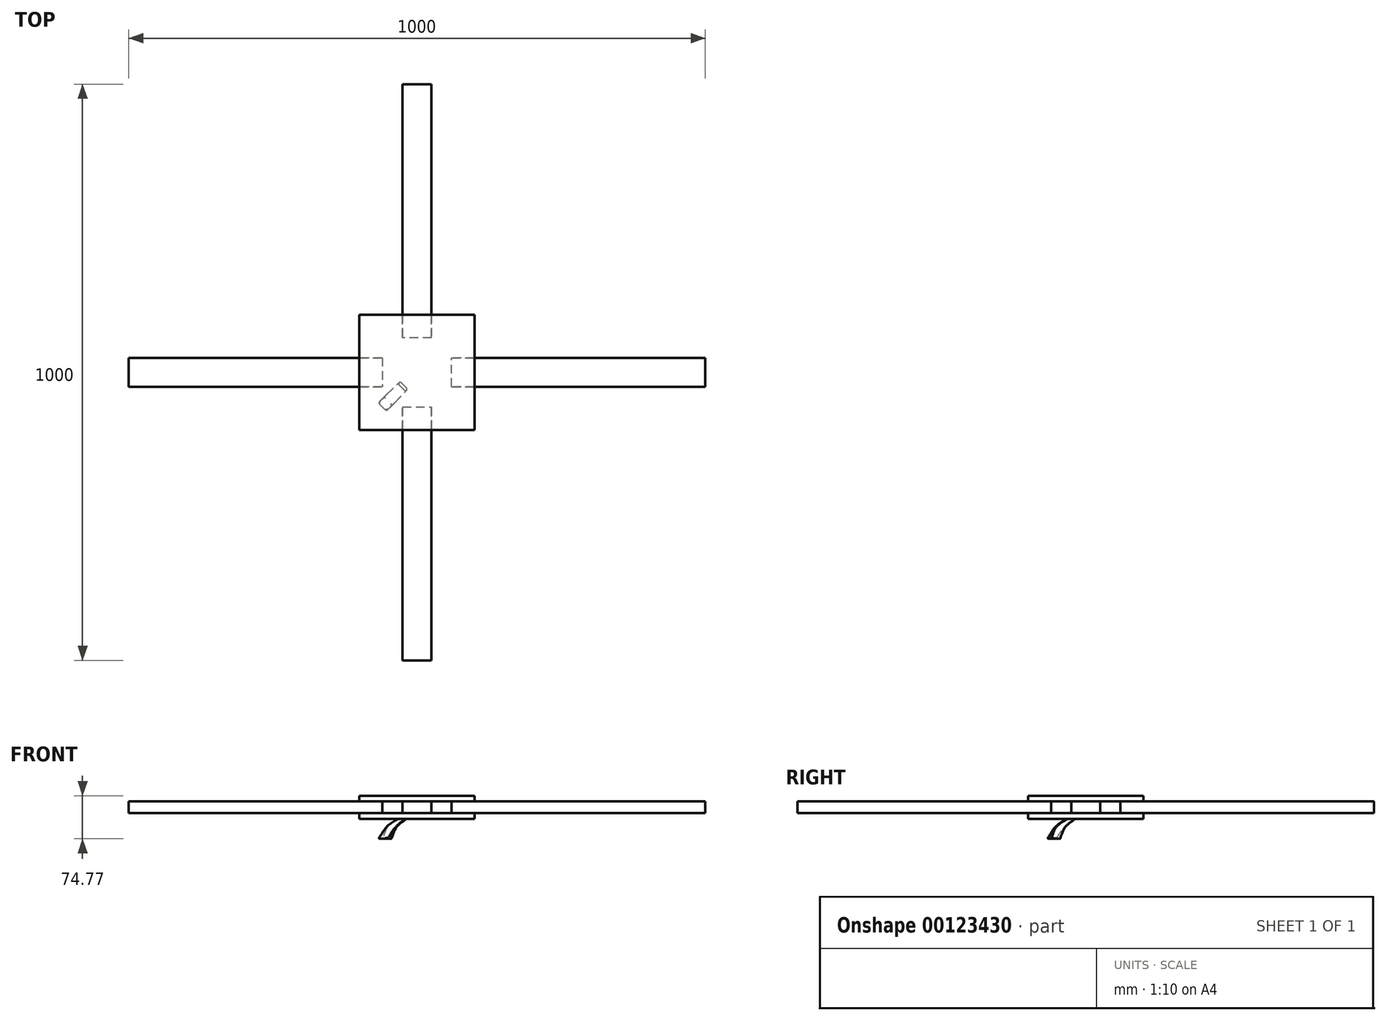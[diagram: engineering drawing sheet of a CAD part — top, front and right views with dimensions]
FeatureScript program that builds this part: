
annotation { "Feature Type Name" : "Feature", "Feature Type Description" : "" }
export const myFeature = defineFeature(function(context is Context, id is Id, definition is map)
    precondition{}
    {
        {
            var Q0;
            Q0=qCreatedBy(makeId("Top.planeOp"),FACE);
            var sketch = newSketch(context, id + "F0", { "sketchPlane" : qUnion([Q0])});
            skLineSegment(sketch, "E0.bottom", {"start": v(100, -100) * mm, "end": v(-100, -100) * mm});
            skLineSegment(sketch, "E0.top", {"start": v(100, 100) * mm, "end": v(-100, 100) * mm});
            skLineSegment(sketch, "E0.left", {"start": v(100, -100) * mm, "end": v(100, 100) * mm});
            skLineSegment(sketch, "E0.right", {"start": v(-100, -100) * mm, "end": v(-100, 100) * mm});
            skPoint(sketch, "E0.middle", {"position": v(0, 0) * mm});
            skSolve(sketch);
        }
        {
            var Q0;
            Q0 = qSketchRegion(id + "F0", true);
            extrude(context, id + "F1", {"entities" : qUnion([Q0]), "depth" : 40 * mm});
        }
        {
            var Q0;
            Q0=makeQuery(id+"F1.opExtrude","SWEPT_FACE",FACE,{"disambiguationData":[OSD([sQuery(id+"F0.wireOp",EDGE,"E0.bottom")])]});
            var sketch = newSketch(context, id + "F2", { "sketchPlane" : qUnion([Q0])});
            skLineSegment(sketch, "E1.bottom", {"start": v(-100, 30) * mm, "end": v(100, 30) * mm});
            skLineSegment(sketch, "E1.top", {"start": v(-100, 10) * mm, "end": v(100, 10) * mm});
            skLineSegment(sketch, "E1.left", {"start": v(-100, 30) * mm, "end": v(-100, 10) * mm});
            skLineSegment(sketch, "E1.right", {"start": v(100, 30) * mm, "end": v(100, 10) * mm});
            skSolve(sketch);
        }
        {
            var Q0;
            Q0 = qSketchRegion(id + "F2", true);
            var Q1;
            Q1=makeQuery(id+"F1.opExtrude","SWEPT_FACE",FACE,{"disambiguationData":[OSD([sQuery(id+"F0.wireOp",EDGE,"E0.top")])]});
            extrude(context, id + "F3", {"entities" : qUnion([Q0]), "operationType" : NewBodyOperationType.REMOVE, "endBound" : BoundingType.UP_TO_SURFACE, "oppositeDirection" : true, "endBoundEntityFace" : qUnion([Q1]), "depth" : 25 * mm});
        }
        {
            var Q0;
            Q0=makeQuery(id+"F3.boolean.opBoolean","COPY",FACE,{"derivedFrom":makeQuery(id+"F3.opExtrude","SWEPT_FACE",FACE,{"disambiguationData":[OSD([sQuery(id+"F2.wireOp",EDGE,"E1.top")])]})});
            var sketch = newSketch(context, id + "F4", { "sketchPlane" : qUnion([Q0])});
            skLineSegment(sketch, "E2.bottom", {"start": v(60, 25) * mm, "end": v(500, 25) * mm});
            skLineSegment(sketch, "E2.top", {"start": v(60, -25) * mm, "end": v(500, -25) * mm});
            skLineSegment(sketch, "E2.left", {"start": v(60, 25) * mm, "end": v(60, -25) * mm});
            skLineSegment(sketch, "E2.right", {"start": v(500, 25) * mm, "end": v(500, -25) * mm});
            skSolve(sketch);
        }
        {
            var Q0;
            Q0 = qSketchRegion(id + "F4", true);
            var Q1;
            Q1=makeQuery(id+"F3.boolean.opBoolean","COPY",FACE,{"derivedFrom":makeQuery(id+"F3.opExtrude","SWEPT_FACE",FACE,{"disambiguationData":[OSD([sQuery(id+"F2.wireOp",EDGE,"E1.bottom")])]})});
            extrude(context, id + "F5", {"entities" : qUnion([Q0]), "endBound" : BoundingType.UP_TO_SURFACE, "endBoundEntityFace" : qUnion([Q1]), "depth" : 25 * mm});
        }
        {
            var Q0;
            Q0=makeQuery(id+"F1.opExtrude","CAP_FACE",FACE,{"disambiguationData":[OSD([sQuery(id+"F0.wireOp",EDGE,"E0.bottom"),sQuery(id+"F0.wireOp",EDGE,"E0.top"),sQuery(id+"F0.wireOp",EDGE,"E0.left"),sQuery(id+"F0.wireOp",EDGE,"E0.right")])],"isStart":false});
            var sketch = newSketch(context, id + "F6", { "sketchPlane" : qUnion([Q0])});
            skCircle(sketch, "E3", {"center": v(0, 0) * mm, "radius": 26.92 * mm});
            skSolve(sketch);
        }
        {
            var Q0;
            Q0=makeQuery(id+"F5.opExtrude","SWEPT_BODY",BODY,{"disambiguationData":[OSD([sQuery(id+"F4.wireOp",EDGE,"E2.bottom"),sQuery(id+"F4.wireOp",EDGE,"E2.top"),sQuery(id+"F4.wireOp",EDGE,"E2.left"),sQuery(id+"F4.wireOp",EDGE,"E2.right")])]});
            var Q1;
            Q1=sQuery(id+"F6.wireOp",EDGE,"E3");
            circularPattern(context, id + "F7", {"entities" : qUnion([Q0]), "axis" : qUnion([Q1]), "angle" : 360 * degree, "instanceCount" : 4, "equalSpace" : true});
        }
        {
            var Q0;
            Q0=makeQuery(id+"F1.opExtrude","CAP_VERTEX",VERTEX,{"disambiguationData":[OSD([sQuery(id+"F0.wireOp",EDGE,"E0.bottom"),sQuery(id+"F0.wireOp",EDGE,"E0.right")])],"isStart":false});
            var Q1;
            Q1=makeQuery(id+"F1.opExtrude","CAP_VERTEX",VERTEX,{"disambiguationData":[OSD([sQuery(id+"F0.wireOp",EDGE,"E0.top"),sQuery(id+"F0.wireOp",EDGE,"E0.left")])],"isStart":false});
            var Q2;
            Q2=qCreatedBy(makeId("Origin.pointOp"),VERTEX);
            cPlane(context, id + "F8", {"entities" : qUnion([Q0, Q1, Q2]), "cplaneType" : CPlaneType.THREE_POINT, "offset" : 25 * mm, "width" : 150 * mm, "height" : 150 * mm});
        }
        {
            var Q0;
            Q0=qCreatedBy(id+"F8.planeOp",FACE);
            var sketch = newSketch(context, id + "F9", { "sketchPlane" : qUnion([Q0])});
            skFitSpline(sketch, "E4", {"points": [v(-37.62, 0) * mm, v(-65.27, -13) * mm, v(-86.01, -34.77) * mm], "startDerivative": vector(-58.46, -21.4) * mm, "endDerivative": vector(-38.3, -48.17) * mm});
            skLineSegment(sketch, "E5", {"start": v(-86.01, -34.77) * mm, "end": v(-70.8, -34.77) * mm});
            skFitSpline(sketch, "E6", {"points": [v(-70.8, -34.77) * mm, v(-59.74, -15.76) * mm, v(-32.43, 0) * mm], "startDerivative": vector(18.43, 44.7) * mm, "endDerivative": vector(57.15, 25.42) * mm});
            skLineSegment(sketch, "E7", {"start": v(-37.62, 0) * mm, "end": v(-32.43, 0) * mm});
            skSolve(sketch);
        }
        {
            var Q0;
            Q0 = qSketchRegion(id + "F9", true);
            extrude(context, id + "F10", {"entities" : qUnion([Q0]), "operationType" : NewBodyOperationType.ADD, "depth" : 10 * mm, "hasSecondDirection" : true, "secondDirectionOppositeDirection" : true, "secondDirectionDepth" : 10 * mm});
        }
        {
            var Q0;
            Q0=makeQuery(id+"F10.opExtrude","CAP_EDGE",EDGE,{"disambiguationData":[OSD([sQuery(id+"F9.wireOp",EDGE,"E4")])],"isStart":false});
            var Q1;
            Q1=makeQuery(id+"F10.opExtrude","CAP_EDGE",EDGE,{"disambiguationData":[OSD([sQuery(id+"F9.wireOp",EDGE,"E4")])],"isStart":true});
            var Q2;
            Q2=makeQuery(id+"F10.opExtrude","CAP_EDGE",EDGE,{"disambiguationData":[OSD([sQuery(id+"F9.wireOp",EDGE,"E6")])],"isStart":false});
            var Q3;
            Q3=makeQuery(id+"F10.opExtrude","CAP_EDGE",EDGE,{"disambiguationData":[OSD([sQuery(id+"F9.wireOp",EDGE,"E6")])],"isStart":true});
            fillet(context, id + "F11", {"entities" : qUnion([Q0, Q1, Q2, Q3]), "radius" : 3 * mm, "tangentPropagation" : true, "allowEdgeOverflow" : false});
        }
        {
            var Q0;
            Q0=makeQuery(id+"F10.opExtrude","SWEPT_FACE",FACE,{"disambiguationData":[OSD([sQuery(id+"F9.wireOp",EDGE,"E5")])]});
            fillet(context, id + "F12", {"entities" : qUnion([Q0]), "radius" : 1 * mm, "tangentPropagation" : true, "allowEdgeOverflow" : false});
        }
        {
            var Q0;
            Q0=makeQuery(id+"F1.opExtrude","CAP_FACE",FACE,{"disambiguationData":[OSD([sQuery(id+"F0.wireOp",EDGE,"E0.bottom"),sQuery(id+"F0.wireOp",EDGE,"E0.top"),sQuery(id+"F0.wireOp",EDGE,"E0.left"),sQuery(id+"F0.wireOp",EDGE,"E0.right")])],"isStart":false});
            var sketch = newSketch(context, id + "F13", { "sketchPlane" : qUnion([Q0])});
            skCircle(sketch, "E8", {"center": v(0, 0) * mm, "radius": 18.33 * mm});
            skSolve(sketch);
        }
    });
